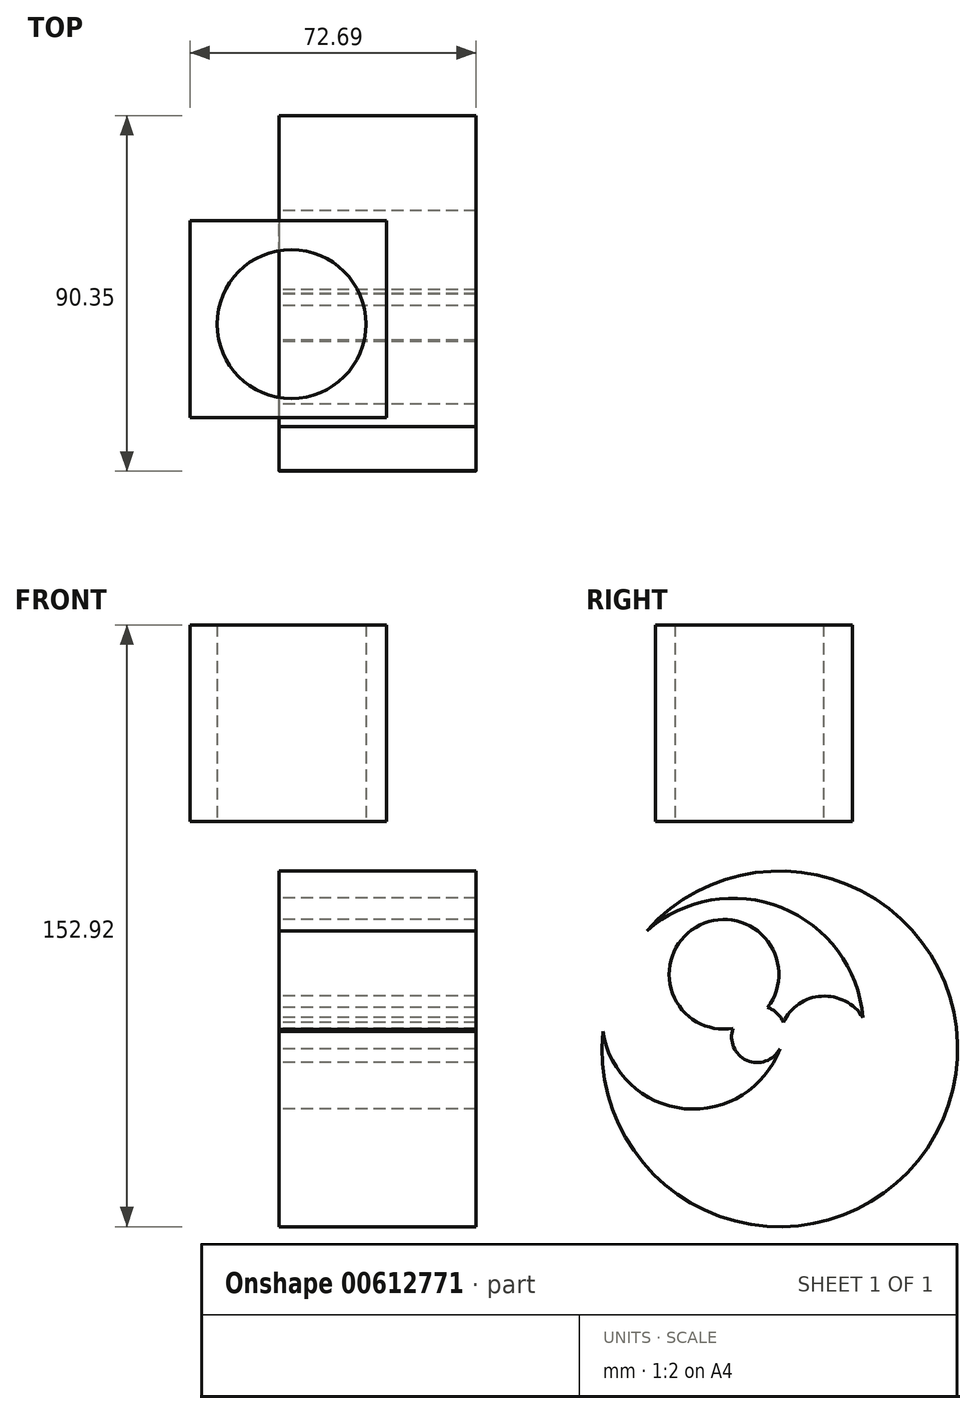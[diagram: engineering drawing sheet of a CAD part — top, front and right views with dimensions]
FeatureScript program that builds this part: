
annotation { "Feature Type Name" : "Feature", "Feature Type Description" : "" }
export const myFeature = defineFeature(function(context is Context, id is Id, definition is map)
    precondition{}
    {
        {
            var Q0;
            Q0=qCreatedBy(makeId("Top.planeOp"),FACE);
            var sketch = newSketch(context, id + "F0", { "sketchPlane" : qUnion([Q0])});
            skLineSegment(sketch, "E0.bottom", {"start": v(-22.69, 26.26) * mm, "end": v(27.31, 26.26) * mm});
            skLineSegment(sketch, "E0.top", {"start": v(-22.69, -23.74) * mm, "end": v(27.31, -23.74) * mm});
            skLineSegment(sketch, "E0.left", {"start": v(-22.69, 26.26) * mm, "end": v(-22.69, -23.74) * mm});
            skLineSegment(sketch, "E0.right", {"start": v(27.31, 26.26) * mm, "end": v(27.31, -23.74) * mm});
            skSolve(sketch);
        }
        {
            var Q0;
            Q0 = qSketchRegion(id + "F0", true);
            extrude(context, id + "F1", {"entities" : qUnion([Q0]), "depth" : 50 * mm, "offsetDistance" : 25 * mm});
        }
        {
            var Q0;
            Q0=qCreatedBy(makeId("Right.planeOp"),FACE);
            var sketch = newSketch(context, id + "F2", { "sketchPlane" : qUnion([Q0])});
            skArc(sketch, "E1", {"start": v(-37.19, -53.35) * mm, "mid": v(49.17, -75.83) * mm, "end": v(-26, -27.73) * mm});
            skArc(sketch, "E2", {"start": v(-37.19, -53.35) * mm, "mid": v(-16.4, -72.95) * mm, "end": v(7.78, -57.74) * mm});
            skArc(sketch, "E3", {"start": v(-37.19, -53.35) * mm, "mid": v(26.23, -65.8) * mm, "end": v(-26, -27.73) * mm});
            skArc(sketch, "E4", {"start": v(4.6, -47.38) * mm, "mid": v(-13.5, -26.82) * mm, "end": v(-4.1, -52.55) * mm});
            skArc(sketch, "E5", {"start": v(30.47, -57.74) * mm, "mid": v(19.12, -44.34) * mm, "end": v(7.78, -57.74) * mm});
            skArc(sketch, "E6", {"start": v(7.78, -57.74) * mm, "mid": v(19.12, -67.09) * mm, "end": v(30.47, -57.74) * mm});
            skArc(sketch, "E7", {"start": v(7.78, -57.74) * mm, "mid": v(5.2, -47.44) * mm, "end": v(-4.1, -52.55) * mm});
            skArc(sketch, "E8", {"start": v(-4.1, -52.55) * mm, "mid": v(-0.57, -60.67) * mm, "end": v(7.78, -57.74) * mm});
            skSolve(sketch);
        }
        {
            var Q0;
            {var subQ0=sQuery(id+"F2.wireOp",EDGE,"E7");var subQ1=sQuery(id+"F2.wireOp",EDGE,"E5");var subQ3=makeQuery(id+"F2.imprint","INTERSECT",VERTEX,{"derivedFrom":[subQ1,subQ0]});Q0=makeQuery(id+"F2.imprint","IMPRINT",FACE,{"disambiguationData":[TD([[makeQuery(id+"F2.imprint","IMPRINT",EDGE,{"disambiguationData":[TD([[subQ3,-1.0]])],"derivedFrom":subQ1}),1.0]])]});}
            var Q1;
            {var subQ0=sQuery(id+"F2.wireOp",EDGE,"E5");var subQ1=sQuery(id+"F2.wireOp",EDGE,"E3");var subQ2=makeQuery(id+"F2.imprint","INTERSECT",VERTEX,{"derivedFrom":[subQ1,subQ0]});Q1=makeQuery(id+"F2.imprint","IMPRINT",FACE,{"disambiguationData":[TD([[makeQuery(id+"F2.imprint","IMPRINT",EDGE,{"disambiguationData":[TD([[subQ2,1.0]])],"derivedFrom":subQ1}),1.0]])]});}
            var Q2;
            {var subQ0=sQuery(id+"F2.wireOp",EDGE,"E8");Q2=makeQuery(id+"F2.imprint","IMPRINT",FACE,{"disambiguationData":[TD([[makeQuery(id+"F2.imprint","IMPRINT",EDGE,{"derivedFrom":subQ0}),1.0]])]});}
            var Q3;
            {var subQ0=sQuery(id+"F2.wireOp",EDGE,"E5");var subQ1=sQuery(id+"F2.wireOp",EDGE,"E3");var subQ2=makeQuery(id+"F2.imprint","INTERSECT",VERTEX,{"derivedFrom":[subQ1,subQ0]});Q3=makeQuery(id+"F2.imprint","IMPRINT",FACE,{"disambiguationData":[TD([[makeQuery(id+"F2.imprint","IMPRINT",EDGE,{"disambiguationData":[TD([[subQ2,1.0]])],"derivedFrom":subQ1}),-1.0]])]});}
            var Q4;
            {var subQ0=sQuery(id+"F2.wireOp",EDGE,"E2");Q4=makeQuery(id+"F2.imprint","IMPRINT",FACE,{"disambiguationData":[TD([[makeQuery(id+"F2.imprint","IMPRINT",EDGE,{"derivedFrom":subQ0}),-1.0]])]});}
            var Q5;
            {var subQ0=sQuery(id+"F2.wireOp",EDGE,"E7");var subQ1=sQuery(id+"F2.wireOp",EDGE,"E4");var subQ3=makeQuery(id+"F2.imprint","INTERSECT",VERTEX,{"derivedFrom":[subQ1,subQ0]});Q5=makeQuery(id+"F2.imprint","IMPRINT",FACE,{"disambiguationData":[TD([[makeQuery(id+"F2.imprint","IMPRINT",EDGE,{"disambiguationData":[TD([[subQ3,-1.0]])],"derivedFrom":subQ1}),1.0]])]});}
            var Q6;
            {var subQ5=sQuery(id+"F2.wireOp",EDGE,"E1");Q6=makeQuery(id+"F2.imprint","IMPRINT",FACE,{"disambiguationData":[TD([[makeQuery(id+"F2.imprint","IMPRINT",EDGE,{"derivedFrom":subQ5}),1.0]])]});}
            extrude(context, id + "F3", {"entities" : qUnion([Q0, Q1, Q2, Q3, Q4, Q5, Q6]), "depth" : 50 * mm, "offsetDistance" : 25 * mm});
        }
        {
            var Q0;
            Q0=qCreatedBy(makeId("Top.planeOp"),FACE);
            var sketch = newSketch(context, id + "F4", { "sketchPlane" : qUnion([Q0])});
            skCircle(sketch, "E9", {"center": v(3.1, 0) * mm, "radius": 18.9 * mm});
            skSolve(sketch);
        }
        {
            var Q0;
            Q0 = qSketchRegion(id + "F4", true);
            extrude(context, id + "F5", {"entities" : qUnion([Q0]), "operationType" : NewBodyOperationType.REMOVE, "depth" : 50 * mm, "offsetDistance" : 25 * mm});
        }
    });
